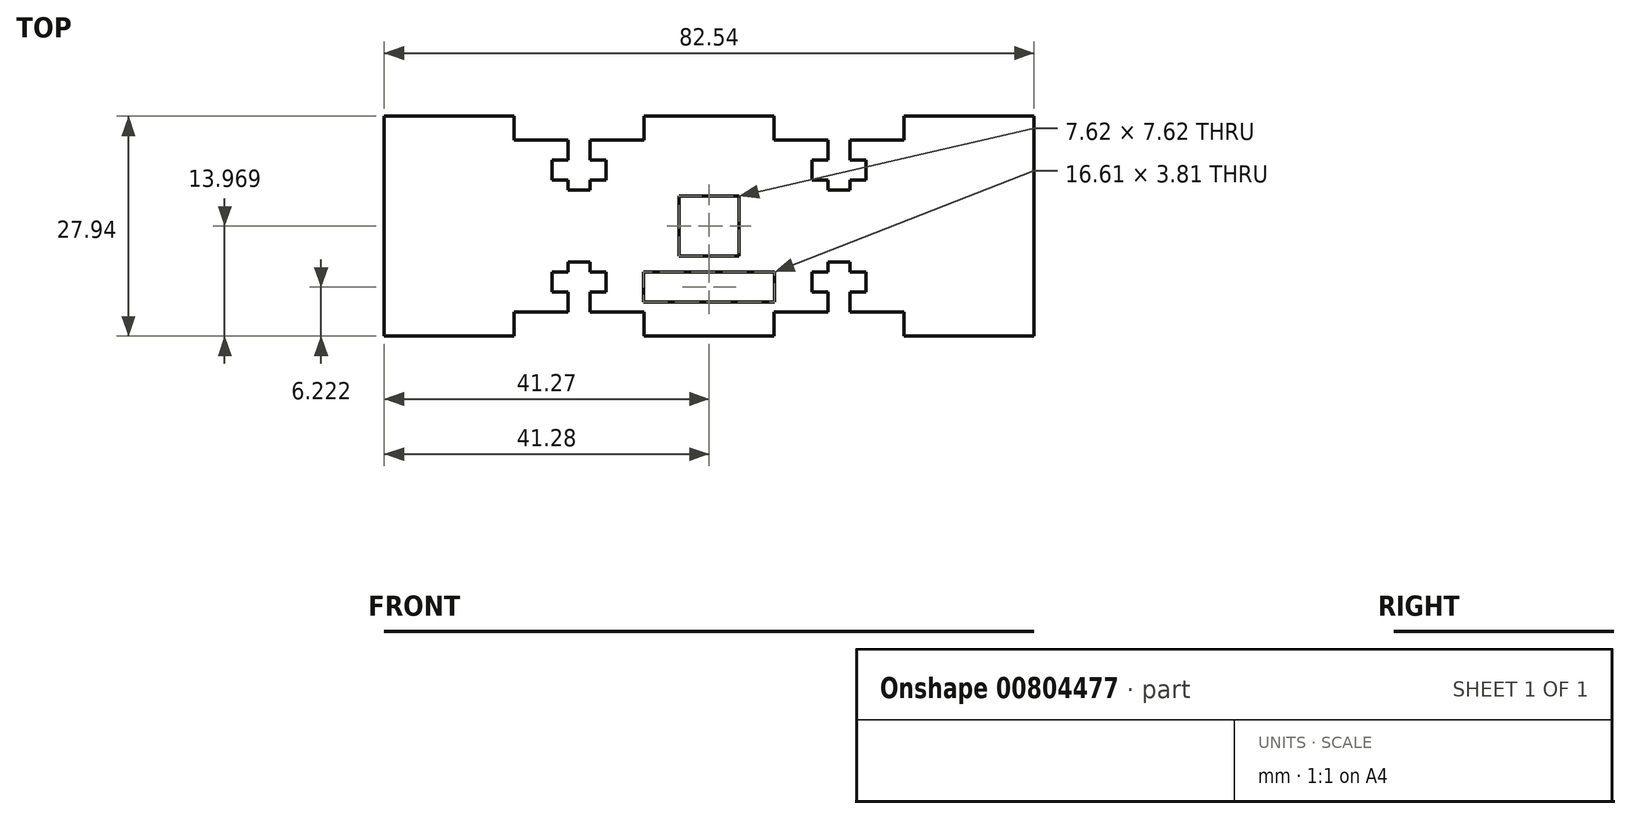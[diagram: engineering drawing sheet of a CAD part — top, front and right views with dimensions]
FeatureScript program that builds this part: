
annotation { "Feature Type Name" : "Feature", "Feature Type Description" : "" }
export const myFeature = defineFeature(function(context is Context, id is Id, definition is map)
    precondition{}
    {
        {
            var Q0;
            Q0=qCreatedBy(makeId("Top.planeOp"),FACE);
            var sketch = newSketch(context, id + "F0", { "sketchPlane" : qUnion([Q0])});
            skLineSegment(sketch, "E0.left", {"start": v(41.27, -8) * mm, "end": v(41.27, 19.94) * mm});
            skLineSegment(sketch, "E0.right", {"start": v(-41.27, -8) * mm, "end": v(-41.27, 19.94) * mm});
            skPoint(sketch, "E0.middle", {"position": v(0, 0) * mm});
            skLineSegment(sketch, "E1", {"start": v(-24.76, -8) * mm, "end": v(-24.76, -4.95) * mm});
            skLineSegment(sketch, "E2", {"start": v(-24.76, -4.95) * mm, "end": v(-17.9, -4.95) * mm});
            skLineSegment(sketch, "E3", {"start": v(-17.9, -4.95) * mm, "end": v(-17.9, -2.41) * mm});
            skLineSegment(sketch, "E4", {"start": v(-17.9, -2.41) * mm, "end": v(-19.94, -2.41) * mm});
            skLineSegment(sketch, "E5", {"start": v(-19.94, -2.41) * mm, "end": v(-19.94, 0.13) * mm});
            skLineSegment(sketch, "E6", {"start": v(-19.94, 0.13) * mm, "end": v(-17.9, 0.13) * mm});
            skLineSegment(sketch, "E7", {"start": v(-17.9, 0.13) * mm, "end": v(-17.9, 1.4) * mm});
            skLineSegment(sketch, "E8", {"start": v(-17.9, 1.4) * mm, "end": v(-15.11, 1.4) * mm});
            skLineSegment(sketch, "E9", {"start": v(-15.11, 1.4) * mm, "end": v(-15.11, 0.13) * mm});
            skLineSegment(sketch, "E10", {"start": v(-15.11, 0.13) * mm, "end": v(-13.08, 0.13) * mm});
            skLineSegment(sketch, "E11", {"start": v(-13.08, 0.13) * mm, "end": v(-13.08, -2.41) * mm});
            skLineSegment(sketch, "E12", {"start": v(-13.08, -2.41) * mm, "end": v(-15.11, -2.41) * mm});
            skLineSegment(sketch, "E13", {"start": v(-15.11, -2.41) * mm, "end": v(-15.11, -4.95) * mm});
            skLineSegment(sketch, "E14", {"start": v(-15.11, -4.95) * mm, "end": v(-8.25, -4.95) * mm});
            skLineSegment(sketch, "E15", {"start": v(-8.25, -4.95) * mm, "end": v(-8.25, -8) * mm});
            skLineSegment(sketch, "E16", {"start": v(-17.9, 0.13) * mm, "end": v(-15.11, 0.13) * mm, "construction": true});
            skLineSegment(sketch, "E17", {"start": v(-17.9, -2.41) * mm, "end": v(-15.11, -2.41) * mm, "construction": true});
            skLineSegment(sketch, "E18", {"start": v(-17.9, -4.95) * mm, "end": v(-15.11, -4.95) * mm, "construction": true});
            skLineSegment(sketch, "E19", {"start": v(-17.9, 0.13) * mm, "end": v(-17.9, -2.41) * mm, "construction": true});
            skLineSegment(sketch, "E20", {"start": v(-15.11, 0.13) * mm, "end": v(-15.11, -2.41) * mm, "construction": true});
            skLineSegment(sketch, "E21.MirrorCS", {"start": v(17.9, 0.13) * mm, "end": v(17.9, -2.41) * mm, "construction": true});
            skLineSegment(sketch, "E22.MirrorCS", {"start": v(15.11, 0.13) * mm, "end": v(15.11, -2.41) * mm, "construction": true});
            skLineSegment(sketch, "E23.MirrorCS", {"start": v(19.94, -2.41) * mm, "end": v(19.94, 0.13) * mm});
            skLineSegment(sketch, "E24.MirrorCS", {"start": v(13.08, 0.13) * mm, "end": v(13.08, -2.41) * mm});
            skLineSegment(sketch, "E25.MirrorCS", {"start": v(15.11, -2.41) * mm, "end": v(15.11, -4.95) * mm});
            skLineSegment(sketch, "E26.MirrorCS", {"start": v(8.25, -4.95) * mm, "end": v(8.25, -8) * mm});
            skLineSegment(sketch, "E27.MirrorCS", {"start": v(17.9, -2.41) * mm, "end": v(15.11, -2.41) * mm, "construction": true});
            skLineSegment(sketch, "E28.MirrorCS", {"start": v(17.9, -4.95) * mm, "end": v(17.9, -2.41) * mm});
            skLineSegment(sketch, "E29.MirrorCS", {"start": v(17.9, -2.41) * mm, "end": v(19.94, -2.41) * mm});
            skLineSegment(sketch, "E30.MirrorCS", {"start": v(24.76, -4.95) * mm, "end": v(17.9, -4.95) * mm});
            skLineSegment(sketch, "E31.MirrorCS", {"start": v(15.11, 1.4) * mm, "end": v(15.11, 0.13) * mm});
            skLineSegment(sketch, "E32.MirrorCS", {"start": v(17.9, -4.95) * mm, "end": v(15.11, -4.95) * mm, "construction": true});
            skLineSegment(sketch, "E33.MirrorCS", {"start": v(19.94, 0.13) * mm, "end": v(17.9, 0.13) * mm});
            skLineSegment(sketch, "E34.MirrorCS", {"start": v(24.76, -8) * mm, "end": v(24.76, -4.95) * mm});
            skLineSegment(sketch, "E35.MirrorCS", {"start": v(17.9, 0.13) * mm, "end": v(15.11, 0.13) * mm, "construction": true});
            skLineSegment(sketch, "E36.MirrorCS", {"start": v(17.9, 1.4) * mm, "end": v(15.11, 1.4) * mm});
            skLineSegment(sketch, "E37.MirrorCS", {"start": v(15.11, 0.13) * mm, "end": v(13.08, 0.13) * mm});
            skLineSegment(sketch, "E38.MirrorCS", {"start": v(15.11, -4.95) * mm, "end": v(8.25, -4.95) * mm});
            skLineSegment(sketch, "E39.MirrorCS", {"start": v(13.08, -2.41) * mm, "end": v(15.11, -2.41) * mm});
            skLineSegment(sketch, "E40.MirrorCS", {"start": v(17.9, 0.13) * mm, "end": v(17.9, 1.4) * mm});
            skLineSegment(sketch, "E41", {"start": v(-41.27, -8) * mm, "end": v(-24.76, -8) * mm});
            skLineSegment(sketch, "E42", {"start": v(-8.25, -8) * mm, "end": v(8.25, -8) * mm});
            skLineSegment(sketch, "E43", {"start": v(24.76, -8) * mm, "end": v(41.27, -8) * mm});
            skLineSegment(sketch, "E44", {"start": v(-41.27, 5.97) * mm, "end": v(41.27, 5.97) * mm, "construction": true});
            skLineSegment(sketch, "E45.MirrorCS", {"start": v(-17.9, 14.35) * mm, "end": v(-15.11, 14.35) * mm, "construction": true});
            skLineSegment(sketch, "E46.MirrorCS", {"start": v(17.9, 14.35) * mm, "end": v(15.11, 14.35) * mm, "construction": true});
            skLineSegment(sketch, "E47.MirrorCS", {"start": v(19.94, 11.81) * mm, "end": v(17.9, 11.81) * mm});
            skLineSegment(sketch, "E48.MirrorCS", {"start": v(-17.9, 14.35) * mm, "end": v(-19.94, 14.35) * mm});
            skLineSegment(sketch, "E49.MirrorCS", {"start": v(17.9, 11.81) * mm, "end": v(17.9, 14.35) * mm, "construction": true});
            skLineSegment(sketch, "E50.MirrorCS", {"start": v(17.9, 11.81) * mm, "end": v(15.11, 11.81) * mm, "construction": true});
            skLineSegment(sketch, "E51.MirrorCS", {"start": v(-17.9, 11.81) * mm, "end": v(-15.11, 11.81) * mm, "construction": true});
            skLineSegment(sketch, "E52.MirrorCS", {"start": v(15.11, 11.81) * mm, "end": v(15.11, 14.35) * mm, "construction": true});
            skLineSegment(sketch, "E53.MirrorCS", {"start": v(-17.9, 11.81) * mm, "end": v(-17.9, 14.35) * mm, "construction": true});
            skLineSegment(sketch, "E54.MirrorCS", {"start": v(-15.11, 11.81) * mm, "end": v(-15.11, 14.35) * mm, "construction": true});
            skLineSegment(sketch, "E55.MirrorCS", {"start": v(-15.11, 11.81) * mm, "end": v(-13.08, 11.81) * mm});
            skLineSegment(sketch, "E56.MirrorCS", {"start": v(17.9, 16.9) * mm, "end": v(15.11, 16.9) * mm, "construction": true});
            skLineSegment(sketch, "E57.MirrorCS", {"start": v(17.9, 16.9) * mm, "end": v(17.9, 14.35) * mm});
            skLineSegment(sketch, "E58.MirrorCS", {"start": v(-17.9, 11.81) * mm, "end": v(-17.9, 10.54) * mm});
            skLineSegment(sketch, "E59.MirrorCS", {"start": v(-15.11, 14.35) * mm, "end": v(-15.11, 16.9) * mm});
            skLineSegment(sketch, "E60.MirrorCS", {"start": v(15.11, 14.35) * mm, "end": v(15.11, 16.9) * mm});
            skLineSegment(sketch, "E61.MirrorCS", {"start": v(-17.9, 16.9) * mm, "end": v(-15.11, 16.9) * mm, "construction": true});
            skLineSegment(sketch, "E62.MirrorCS", {"start": v(-17.9, 16.9) * mm, "end": v(-17.9, 14.35) * mm});
            skLineSegment(sketch, "E63.MirrorCS", {"start": v(15.11, 11.81) * mm, "end": v(13.08, 11.81) * mm});
            skLineSegment(sketch, "E64.MirrorCS", {"start": v(-19.94, 14.35) * mm, "end": v(-19.94, 11.81) * mm});
            skLineSegment(sketch, "E65.MirrorCS", {"start": v(-13.08, 11.81) * mm, "end": v(-13.08, 14.35) * mm});
            skLineSegment(sketch, "E66.MirrorCS", {"start": v(13.08, 11.81) * mm, "end": v(13.08, 14.35) * mm});
            skLineSegment(sketch, "E67.MirrorCS", {"start": v(24.76, 19.94) * mm, "end": v(24.76, 16.9) * mm});
            skLineSegment(sketch, "E68.MirrorCS", {"start": v(19.94, 14.35) * mm, "end": v(19.94, 11.81) * mm});
            skLineSegment(sketch, "E69.MirrorCS", {"start": v(-8.25, 16.9) * mm, "end": v(-8.25, 19.94) * mm});
            skLineSegment(sketch, "E70.MirrorCS", {"start": v(17.9, 11.81) * mm, "end": v(17.9, 10.54) * mm});
            skLineSegment(sketch, "E71.MirrorCS", {"start": v(-15.11, 10.54) * mm, "end": v(-15.11, 11.81) * mm});
            skLineSegment(sketch, "E72.MirrorCS", {"start": v(13.08, 14.35) * mm, "end": v(15.11, 14.35) * mm});
            skLineSegment(sketch, "E73.MirrorCS", {"start": v(-19.94, 11.81) * mm, "end": v(-17.9, 11.81) * mm});
            skLineSegment(sketch, "E74.MirrorCS", {"start": v(8.25, 16.9) * mm, "end": v(8.25, 19.94) * mm});
            skLineSegment(sketch, "E75.MirrorCS", {"start": v(17.9, 10.54) * mm, "end": v(15.11, 10.54) * mm});
            skLineSegment(sketch, "E76.MirrorCS", {"start": v(15.11, 10.54) * mm, "end": v(15.11, 11.81) * mm});
            skLineSegment(sketch, "E77.MirrorCS", {"start": v(-24.77, 19.94) * mm, "end": v(-24.77, 16.9) * mm});
            skLineSegment(sketch, "E78.MirrorCS", {"start": v(-17.9, 10.54) * mm, "end": v(-15.11, 10.54) * mm});
            skLineSegment(sketch, "E79.MirrorCS", {"start": v(17.9, 14.35) * mm, "end": v(19.94, 14.35) * mm});
            skLineSegment(sketch, "E80.MirrorCS", {"start": v(-13.08, 14.35) * mm, "end": v(-15.11, 14.35) * mm});
            skLineSegment(sketch, "E81.MirrorCS", {"start": v(-8.26, 19.94) * mm, "end": v(8.25, 19.94) * mm});
            skLineSegment(sketch, "E82.MirrorCS", {"start": v(-24.77, 16.9) * mm, "end": v(-17.9, 16.9) * mm});
            skPoint(sketch, "E83.MirrorP", {"position": v(0, 11.94) * mm});
            skLineSegment(sketch, "E84.MirrorCS", {"start": v(-15.11, 16.9) * mm, "end": v(-8.26, 16.9) * mm});
            skLineSegment(sketch, "E85.MirrorCS", {"start": v(15.11, 16.9) * mm, "end": v(8.25, 16.9) * mm});
            skLineSegment(sketch, "E86.MirrorCS", {"start": v(24.76, 16.9) * mm, "end": v(17.9, 16.9) * mm});
            skLineSegment(sketch, "E87.MirrorCS", {"start": v(24.76, 19.94) * mm, "end": v(41.27, 19.94) * mm});
            skLineSegment(sketch, "E88.MirrorCS", {"start": v(-41.28, 19.94) * mm, "end": v(-24.77, 19.94) * mm});
            skLineSegment(sketch, "E89", {"start": v(0, 19.94) * mm, "end": v(0, -8) * mm, "construction": true});
            skLineSegment(sketch, "E90.bottom", {"start": v(3.81, 2.16) * mm, "end": v(-3.81, 2.16) * mm});
            skLineSegment(sketch, "E90.top", {"start": v(3.81, 9.78) * mm, "end": v(-3.8, 9.78) * mm});
            skLineSegment(sketch, "E90.left", {"start": v(3.81, 2.16) * mm, "end": v(3.81, 9.78) * mm});
            skLineSegment(sketch, "E90.right", {"start": v(-3.81, 2.16) * mm, "end": v(-3.8, 9.78) * mm});
            skPoint(sketch, "E90.middle", {"position": v(0, 5.97) * mm});
            skLineSegment(sketch, "E91.bottom", {"start": v(-8.3, -3.68) * mm, "end": v(8.32, -3.68) * mm});
            skLineSegment(sketch, "E91.top", {"start": v(-8.3, 0.13) * mm, "end": v(8.32, 0.13) * mm});
            skLineSegment(sketch, "E91.left", {"start": v(-8.3, -3.68) * mm, "end": v(-8.3, 0.13) * mm});
            skLineSegment(sketch, "E91.right", {"start": v(8.32, -3.68) * mm, "end": v(8.32, 0.13) * mm});
            skSolve(sketch);
        }
        {
            var Q0;
            {var subQ5=sQuery(id+"F0.wireOp",EDGE,"E0.left");Q0=makeQuery(id+"F0.imprint","IMPRINT",FACE,{"disambiguationData":[TD([[makeQuery(id+"F0.imprint","IMPRINT",EDGE,{"derivedFrom":subQ5}),1.0]])]});}
            var Q1;
            {var subQ1=sQuery(id+"F0.wireOp",EDGE,"CzhvGjKk-29w6-T0OR-dwu9-fqJqds6kPYbs");Q1=makeQuery(id+"F0.imprint","IMPRINT",FACE,{"disambiguationData":[TD([[makeQuery(id+"F0.imprint","IMPRINT",EDGE,{"derivedFrom":subQ1}),-1.0]])]});}
            var Q2;
            {var subQ1=sQuery(id+"F0.wireOp",EDGE,"b7c2914f-3dff-48f9-a288-cf792061c99c1.MirrorCS");Q2=makeQuery(id+"F0.imprint","IMPRINT",FACE,{"disambiguationData":[TD([[makeQuery(id+"F0.imprint","IMPRINT",EDGE,{"derivedFrom":subQ1}),1.0]])]});}
            extrude(context, id + "F1", {"entities" : qUnion([Q0, Q1, Q2]), "depth" : 1 / 203.2 * mm, "offsetDistance" : 25.4 * mm});
        }
    });
